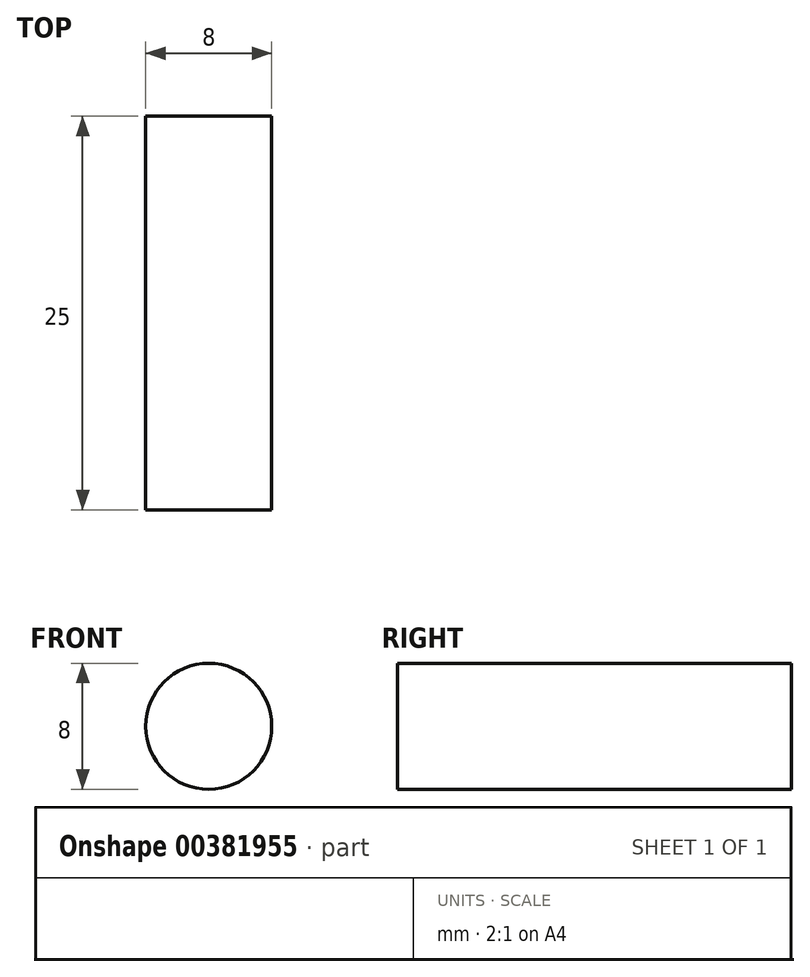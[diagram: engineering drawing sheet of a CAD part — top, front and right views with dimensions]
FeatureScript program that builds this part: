
annotation { "Feature Type Name" : "Feature", "Feature Type Description" : "" }
export const myFeature = defineFeature(function(context is Context, id is Id, definition is map)
    precondition{}
    {
        {
            var Q0;
            Q0=qCreatedBy(makeId("Front.planeOp"),FACE);
            var sketch = newSketch(context, id + "F0", { "sketchPlane" : qUnion([Q0])});
            skCircle(sketch, "E0", {"center": v(0, 0) * mm, "radius": 4 * mm});
            skSolve(sketch);
        }
        {
            var Q0;
            Q0=qSketchRegion(id+"F0",true);
            extrude(context, id + "F1", {"entities" : qUnion([Q0]), "endBound" : BoundingType.SYMMETRIC, "depth" : 25 * mm});
        }
    });
